# Revit family: IS_Connect_T9924_BIM_IT
name_source: partatom
category: Plumbing Fixtures
units: mm (PartAtom-declared; Revit-internal decimal feet)

## family parameters
Always vertical = No
Cut with Voids When Loaded = No
OmniClass Number = 23.45.05.14.21.11
OmniClass Title = Bath/Shower Units
Part Type = Normal
Room Calculation Point = No
Round Connector Dimension = Use Diameter
Shared = No
Work Plane-Based = No

## types (2) — shared parameters
Accessori = https://www.idealstandard.it
Aiuto = https://www.idealstandard.it
Autore = Ideal Standard
BIMobject category = Shower screens
BIMobject category code = sanitary-shower-screens
BIMobject main category = Sanitary
BIMobject main category code = sanitary
BOSUseNativeGeometries = 1
Brand = Ideal Standard
Brand url = http://www.idealstandard.it
Caratteristiche = CONNECT 2, SCHERMO VASCA 80X80 VETRO TRASPARENTE
CodiceDiPrestazione = EN
Connessione = piombatura
Description = Connect- V1/80 - Parete doccia per vasca - Vetro temperato trasparente -  Versione angolo stondato - Profilo Brill lucido
DescrizioneClassifcazioneUni2015 = Shower enclosures
Desrizione = Connect- V1/80 - Parete doccia per vasca - Vetro temperato trasparente -  Versione angolo stondato - Profilo Brill lucido
Dimensione = 1900 x 720 x 90mm
EAN code = https://8014140383253
Forma = Rectangolare
Garanzia = Garanzia Ideal Standard
Grado = n/s
IFC Classification = IfcSanitaryTerminal
IfcEsportaCome = FurnitureType
InformazioniDiProdotto = https://www.idealstandard.it
Installation instructions = https://www.idealstandard.it
Installazione = http://www.idealstandard.it
InstruzioniInstallazione = https://www.idealstandard.it
LarghezzaNominale = 826 mm
LunghezzaNominale = 50 mm  [stored 0.164042 ft]
Maniglia = No
Manufacturer name = Ideal Standard
Material main = Glass
Materiale = Glass
NBS Reference Code = 46-35-70/332
NBS Reference Description = Shower Enclosures
Nome = ShowerEnclosure_Connect2_T9924_IdealStandard
NomeOggettoBim = ISI_IdealStandard_ShowersEnclosures_Connect2_T9924
NominalHeight = 1403 mm
NominalLength = 50 mm  [stored 0.164042 ft]
NominalWidth = 826 mm
NumeroDiModello = T9922EO
OmniClass Code = 23-31 17 00
OmniClass Description = Showers
PartiDiRicambio = https://www.idealstandard.it
PesoNetto = 22
PiattoDoccia = No
Product Guid = 01809f17-fe67-4f28-982d-f5c676086560
Product SKU = T9924
Product certification = http://www.idealstandard.it
Product data url = https://bimobject.com
Product family = Sanitary
Product group = Shower enclosures
Product url = https://www.idealstandard.it
QR code = http://bimobject.com
RiferimentoClassificazioneUni2015 = Pr_40_20_06_79
Size = 1900 x 720 x 90mm
Technical description = https://www.idealstandard.it
Telefono = 800 652 290
TipoDiDato = Fisso
TipoEspotazioneIfc = SHOWER
URL = https://www.idealstandard.it
Uniclass 1.4 Code = L72142
Uniclass 1.4 Description = Shower screens, curtains
Uniclass 2.0 Code = PR-35-06-79
Uniclass 2.0 Description = Shower Enclosures
Uniclass 2015 Code = Pr_40_20_06_79
Uniclass 2015 Name = Shower enclosures
UnitàDurata = anni
UnitàDurataGaranzia = anni
UnitàLineare = millimetri
UnitàMonetaria = €
UnitàSuperficie = €
UnitàVolume = millimetri
Versione = 1
VersioneClassificazioneUni2015 = 1
Youtube clip = https://www.youtube.com
zero-valued in all types: AltezzaNominale, CostoDiSostituzione, DimensioneScarico, Nominal depth, Nominal height, ProfonditaNominale, SeatMaterial, SpessoreDelMateriale, SpilloverLivello, Weight Net (Kg)

## per-type parameters (varying)
| type | CodiceABarre | Colore | Date of publishing | Edition number | Finitura | Model | ModelloDiRiferimento | Product name | Revisione | Riferimento |
| T9924V3 - CONNECT 2 BATH SCREEN 80X80 CLEAR GLASS - MATT BLACK | 8014140483984 | NERO OPACO | 18/05/2021 | 1 | NERO OPACO | T9924V3 | T9924V3 | CONNECT 2, BATH SCREEN 80X80 CLEAR GLASS  -  MATT BLACK | 1 | CONNECT 2, BATH SCREEN 80X80 CLEAR GLASS  -  MATT BLACK |
| T9924EO - CONNECT 2 BATH SCREEN 80X80 CLEAR GLASS - SILVER | 8014140383253 | ARGENTO | 2019_01_04 | 2 | ARGENTO | T9924EO | T9924EO | CONNECT 2, BATH SCREEN 80X80 CLEAR GLASS  -  SILVER | 2 | CONNECT 2, BATH SCREEN 80X80 CLEAR GLASS  -  SILVER |

note: [stored X ft] marks values corroborated as IEEE doubles in the binary element streams (Revit-internal decimal feet)

## geometry (parser evidence)
native form markers: Sweep x3
no freeform markers — native parametric forms only
